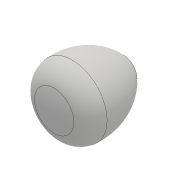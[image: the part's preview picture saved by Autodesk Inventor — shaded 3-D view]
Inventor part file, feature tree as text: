
AUTODESK INVENTOR PART (.ipt)
format: ipt  version: 2017 (Build 210142000, 142)  size: 134,144 bytes
history: native  units: mm
features: fillet x2, revolve x1, sketch x1
ambient origin geometry x8: Origin, YZ Plane, XZ Plane, XY Plane, X Axis, Y Axis, Z Axis, Center Point
bodies: Solid1 (feature_tree)
feature tree (4):
  revolve  "Revolution1"  [1 undecoded]
  fillet  "Fillet1"  Radius=80.0mm
  fillet  "Fillet2"  Radius=4.0mm
  sketch  "Sketch1"  dims[d0=32.0mm d1=32.0mm d2=80.0mm d3=4.0mm d4=90.0deg d5=20.0mm d6=20.0mm]
note: 1 required parameter value undecoded (feature->parameter linkage not recoverable at this tier; creation-order binding heuristic only, values carry confidence <= 0.55)
